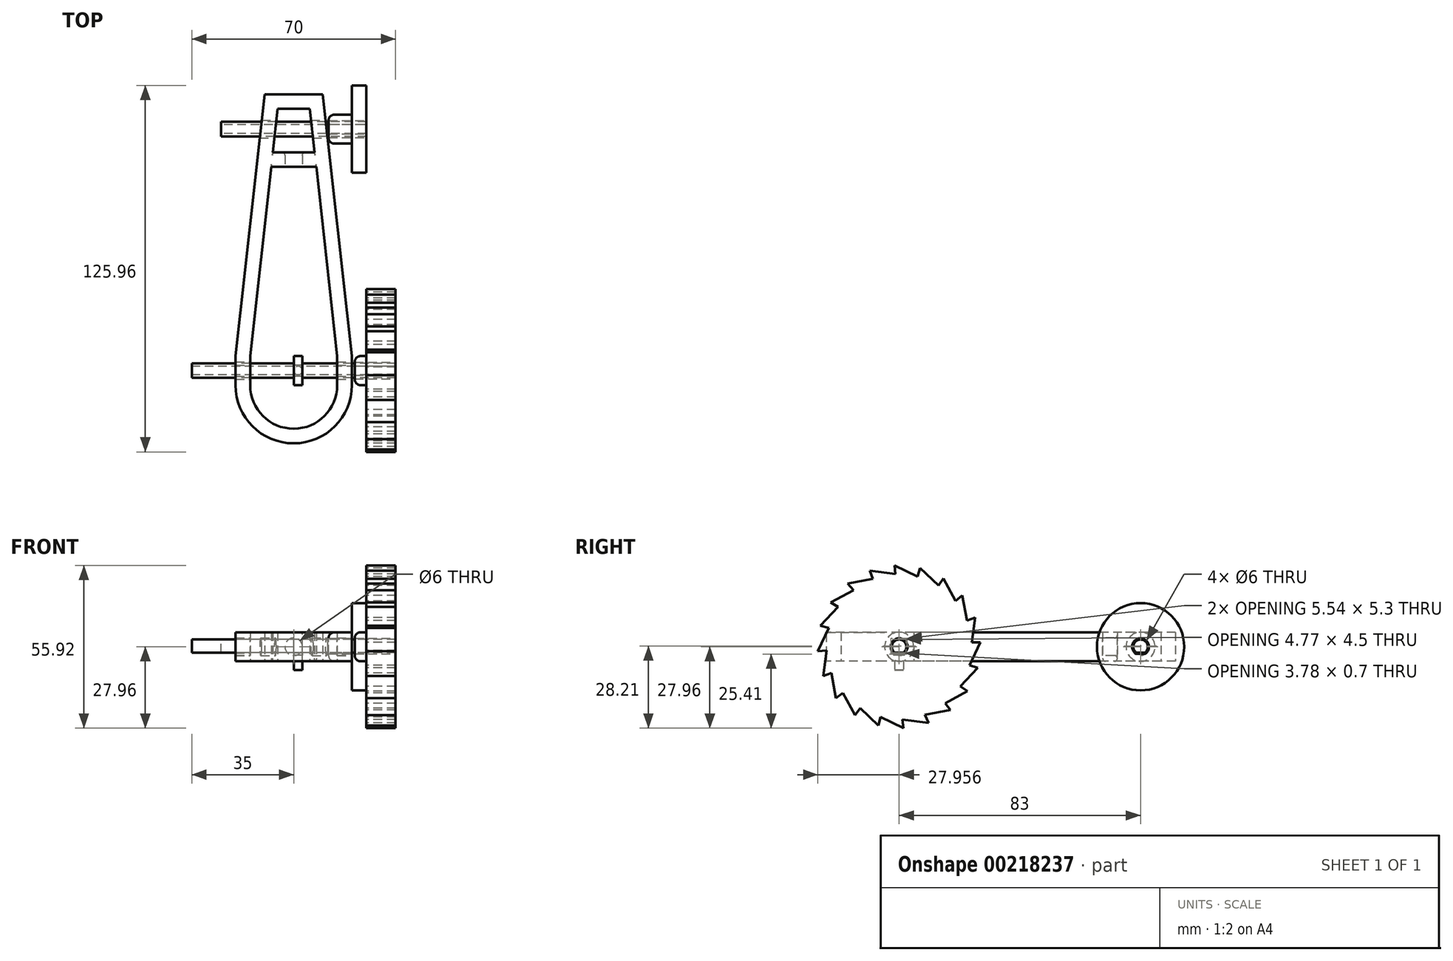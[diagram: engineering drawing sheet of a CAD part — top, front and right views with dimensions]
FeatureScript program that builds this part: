
annotation { "Feature Type Name" : "Feature", "Feature Type Description" : "" }
export const myFeature = defineFeature(function(context is Context, id is Id, definition is map)
    precondition{}
    {
        {
            var Q0;
            Q0=qCreatedBy(makeId("Top.planeOp"),FACE);
            var sketch = newSketch(context, id + "F0", { "sketchPlane" : qUnion([Q0])});
            skLineSegment(sketch, "E0.bottom", {"start": v(-20, -34.15) * mm, "end": v(20, -34.15) * mm});
            skLineSegment(sketch, "E0.top", {"start": v(-20, -44.15) * mm, "end": v(20, -44.15) * mm});
            skLineSegment(sketch, "E0.left", {"start": v(-20, -34.15) * mm, "end": v(-20, -44.15) * mm});
            skLineSegment(sketch, "E0.right", {"start": v(20, -34.15) * mm, "end": v(20, -44.15) * mm});
            skLineSegment(sketch, "E1.bottom", {"start": v(-10, 55.85) * mm, "end": v(10, 55.85) * mm});
            skLineSegment(sketch, "E1.top", {"start": v(-10, 50.85) * mm, "end": v(10, 50.85) * mm});
            skLineSegment(sketch, "E1.left", {"start": v(-10, 55.85) * mm, "end": v(-10, 50.85) * mm});
            skLineSegment(sketch, "E1.right", {"start": v(10, 55.85) * mm, "end": v(10, 50.85) * mm});
            skPoint(sketch, "E2", {"position": v(0, -34.15) * mm});
            skPoint(sketch, "E3", {"position": v(0, 50.85) * mm});
            skLineSegment(sketch, "E4", {"start": v(-10, 55.85) * mm, "end": v(-20, -34.15) * mm});
            skLineSegment(sketch, "E5", {"start": v(10, 55.85) * mm, "end": v(20, -34.15) * mm});
            skLineSegment(sketch, "E6", {"start": v(-5.52, 50.85) * mm, "end": v(-14.97, -34.15) * mm});
            skLineSegment(sketch, "E7", {"start": v(5.52, 50.85) * mm, "end": v(14.97, -34.15) * mm});
            skLineSegment(sketch, "E8.bottom", {"start": v(-7.75, 30.85) * mm, "end": v(7.75, 30.85) * mm});
            skLineSegment(sketch, "E8.top", {"start": v(-7.75, 35.85) * mm, "end": v(7.75, 35.85) * mm});
            skLineSegment(sketch, "E8.left", {"start": v(-7.75, 30.85) * mm, "end": v(-7.75, 35.85) * mm});
            skLineSegment(sketch, "E8.right", {"start": v(7.75, 30.85) * mm, "end": v(7.75, 35.85) * mm});
            skArc(sketch, "E9", {"start": v(-20, -44.15) * mm, "mid": v(0, -64.15) * mm, "end": v(20, -44.15) * mm});
            skLineSegment(sketch, "E10", {"start": v(-14.97, -34.15) * mm, "end": v(-14.97, -44.15) * mm});
            skLineSegment(sketch, "E11", {"start": v(14.97, -34.15) * mm, "end": v(14.97, -44.15) * mm});
            skArc(sketch, "E12", {"start": v(-14.97, -44.15) * mm, "mid": v(0, -59.12) * mm, "end": v(14.97, -44.15) * mm});
            skSolve(sketch);
        }
        {
            var Q0;
            {var subQ0=sQuery(id+"F0.wireOp",EDGE,"E0.left");Q0=makeQuery(id+"F0.imprint","IMPRINT",FACE,{"disambiguationData":[TD([[makeQuery(id+"F0.imprint","IMPRINT",EDGE,{"derivedFrom":subQ0}),1.0]])]});}
            var Q1;
            {var subQ0=sQuery(id+"F0.wireOp",EDGE,"E0.right");Q1=makeQuery(id+"F0.imprint","IMPRINT",FACE,{"disambiguationData":[TD([[makeQuery(id+"F0.imprint","IMPRINT",EDGE,{"derivedFrom":subQ0}),-1.0]])]});}
            var Q2;
            Q2=makeQuery(id+"F0.imprint","IMPRINT",FACE,{"disambiguationData":[TD([[makeQuery(id+"F0.imprint","IMPRINT",EDGE,{"derivedFrom":sQuery(id+"F0.wireOp",EDGE,"E1.bottom")}),-1.0]])]});
            var Q3;
            {var subQ1=sQuery(id+"F0.wireOp",EDGE,"E1.right");Q3=makeQuery(id+"F0.imprint","IMPRINT",FACE,{"disambiguationData":[TD([[makeQuery(id+"F0.imprint","IMPRINT",EDGE,{"derivedFrom":subQ1}),1.0]])]});}
            var Q4;
            {var subQ5=sQuery(id+"F0.wireOp",EDGE,"E1.left");Q4=makeQuery(id+"F0.imprint","IMPRINT",FACE,{"disambiguationData":[TD([[makeQuery(id+"F0.imprint","IMPRINT",EDGE,{"derivedFrom":subQ5}),-1.0]])]});}
            var Q5;
            {var subQ0=sQuery(id+"F0.wireOp",EDGE,"E8.bottom");Q5=makeQuery(id+"F0.imprint","IMPRINT",FACE,{"disambiguationData":[TD([[makeQuery(id+"F0.imprint","IMPRINT",EDGE,{"derivedFrom":subQ0}),1.0]])]});}
            var Q6;
            {var subQ0=sQuery(id+"F0.wireOp",EDGE,"E8.left");Q6=makeQuery(id+"F0.imprint","IMPRINT",FACE,{"disambiguationData":[TD([[makeQuery(id+"F0.imprint","IMPRINT",EDGE,{"derivedFrom":subQ0}),-1.0]])]});}
            var Q7;
            {var subQ0=sQuery(id+"F0.wireOp",EDGE,"E8.right");Q7=makeQuery(id+"F0.imprint","IMPRINT",FACE,{"disambiguationData":[TD([[makeQuery(id+"F0.imprint","IMPRINT",EDGE,{"derivedFrom":subQ0}),1.0]])]});}
            var Q8;
            {var subQ0=sQuery(id+"F0.wireOp",EDGE,"E9");Q8=makeQuery(id+"F0.imprint","IMPRINT",FACE,{"disambiguationData":[TD([[makeQuery(id+"F0.imprint","IMPRINT",EDGE,{"derivedFrom":subQ0}),1.0]])]});}
            extrude(context, id + "F1", {"entities" : qUnion([Q0, Q1, Q2, Q3, Q4, Q5, Q6, Q7, Q8]), "depth" : 10 * mm});
        }
        {
            var Q0;
            Q0=qCreatedBy(makeId("Right.planeOp"),FACE);
            var sketch = newSketch(context, id + "F2", { "sketchPlane" : qUnion([Q0])});
            skCircle(sketch, "E13", {"center": v(43.85, 5) * mm, "radius": 3 * mm});
            skCircle(sketch, "E14", {"center": v(-39.15, 5) * mm, "radius": 3 * mm});
            skCircle(sketch, "E15", {"center": v(-39.15, 5) * mm, "radius": 2.5 * mm});
            skLineSegment(sketch, "E16", {"start": v(-40.65, 3) * mm, "end": v(-37.65, 3) * mm});
            skCircle(sketch, "E17", {"center": v(43.85, 5) * mm, "radius": 2.5 * mm});
            skLineSegment(sketch, "E18", {"start": v(42.35, 3) * mm, "end": v(45.35, 3) * mm});
            skCircle(sketch, "E19", {"center": v(-39.15, 5) * mm, "radius": 5 * mm});
            skCircle(sketch, "E20", {"center": v(-39.15, 5) * mm, "radius": 2.9 * mm});
            skLineSegment(sketch, "E21", {"start": v(-37.26, 2.8) * mm, "end": v(-41.04, 2.8) * mm});
            skSolve(sketch);
        }
        {
            var Q0;
            Q0=makeQuery(id+"F2.imprint","IMPRINT",FACE,{"disambiguationData":[TD([[makeQuery(id+"F2.imprint","IMPRINT",EDGE,{"derivedFrom":sQuery(id+"F2.wireOp",EDGE,"E14")}),1.0]])]});
            var Q1;
            Q1=makeQuery(id+"F2.imprint","IMPRINT",FACE,{"disambiguationData":[TD([[makeQuery(id+"F2.imprint","IMPRINT",EDGE,{"derivedFrom":sQuery(id+"F2.wireOp",EDGE,"E13")}),1.0]])]});
            var Q2;
            {var subQ0=sQuery(id+"F2.wireOp",EDGE,"E16");Q2=makeQuery(id+"F2.imprint","IMPRINT",FACE,{"disambiguationData":[TD([[makeQuery(id+"F2.imprint","IMPRINT",EDGE,{"derivedFrom":subQ0}),1.0]])]});}
            var Q3;
            {var subQ0=sQuery(id+"F2.wireOp",EDGE,"E18");Q3=makeQuery(id+"F2.imprint","IMPRINT",FACE,{"disambiguationData":[TD([[makeQuery(id+"F2.imprint","IMPRINT",EDGE,{"derivedFrom":subQ0}),1.0]])]});}
            var Q4;
            {var subQ0=sQuery(id+"F2.wireOp",EDGE,"E18");Q4=makeQuery(id+"F2.imprint","IMPRINT",FACE,{"disambiguationData":[TD([[makeQuery(id+"F2.imprint","IMPRINT",EDGE,{"derivedFrom":subQ0}),-1.0]])]});}
            var Q5;
            {var subQ0=sQuery(id+"F2.wireOp",EDGE,"E16");var subQ1=sQuery(id+"F2.wireOp",EDGE,"E15");var subQ2=makeQuery(id+"F2.imprint","INTERSECT",VERTEX,{"disambiguationData":[OD(0.0)],"derivedFrom":[subQ1,subQ0]});Q5=makeQuery(id+"F2.imprint","IMPRINT",FACE,{"disambiguationData":[TD([[makeQuery(id+"F2.imprint","IMPRINT",EDGE,{"disambiguationData":[TD([[subQ2,-1.0]])],"derivedFrom":subQ1}),-1.0]])]});}
            var Q6;
            {var subQ0=sQuery(id+"F2.wireOp",EDGE,"E16");Q6=makeQuery(id+"F2.imprint","IMPRINT",FACE,{"disambiguationData":[TD([[makeQuery(id+"F2.imprint","IMPRINT",EDGE,{"derivedFrom":subQ0}),-1.0]])]});}
            var Q7;
            {var subQ0=sQuery(id+"F2.wireOp",EDGE,"E21");var subQ1=sQuery(id+"F2.wireOp",EDGE,"E15");var subQ2=makeQuery(id+"F2.imprint","INTERSECT",VERTEX,{"disambiguationData":[OD(0.0)],"derivedFrom":[subQ1,subQ0]});Q7=makeQuery(id+"F2.imprint","IMPRINT",FACE,{"disambiguationData":[TD([[makeQuery(id+"F2.imprint","IMPRINT",EDGE,{"disambiguationData":[TD([[subQ2,-1.0]])],"derivedFrom":subQ1}),-1.0]])]});}
            var Q8;
            {var subQ0=sQuery(id+"F2.wireOp",EDGE,"E21");var subQ1=sQuery(id+"F2.wireOp",EDGE,"E15");var subQ2=makeQuery(id+"F2.imprint","INTERSECT",VERTEX,{"disambiguationData":[OD(0.0)],"derivedFrom":[subQ1,subQ0]});Q8=makeQuery(id+"F2.imprint","IMPRINT",FACE,{"disambiguationData":[TD([[makeQuery(id+"F2.imprint","IMPRINT",EDGE,{"disambiguationData":[TD([[subQ2,-1.0]])],"derivedFrom":subQ1}),1.0]])]});}
            extrude(context, id + "F3", {"entities" : qUnion([Q0, Q1, Q2, Q3, Q4, Q5, Q6, Q7, Q8]), "operationType" : NewBodyOperationType.REMOVE, "oppositeDirection" : true, "depth" : 25 * mm, "hasSecondDirection" : true, "secondDirectionOppositeDirection" : false, "secondDirectionDepth" : 25 * mm});
        }
        {
            var Q0;
            Q0=makeQuery(id+"F1.opExtrude","SWEPT_FACE",FACE,{"disambiguationData":[OSD([sQuery(id+"F0.wireOp",EDGE,"E8.bottom")])]});
            var sketch = newSketch(context, id + "F4", { "sketchPlane" : qUnion([Q0])});
            skCircle(sketch, "E22", {"center": v(0, 5) * mm, "radius": 3 * mm});
            skPoint(sketch, "E22.centerSnap0", {"position": v(-7.75, 5) * mm});
            skSolve(sketch);
        }
        {
            var Q0;
            Q0=makeQuery(id+"F4.imprint","IMPRINT",FACE,{"disambiguationData":[TD([[makeQuery(id+"F4.imprint","IMPRINT",EDGE,{"derivedFrom":sQuery(id+"F4.wireOp",EDGE,"E22")}),1.0]])]});
            extrude(context, id + "F5", {"entities" : qUnion([Q0]), "operationType" : NewBodyOperationType.REMOVE, "oppositeDirection" : true, "depth" : 6 * mm});
        }
        {
            var Q0;
            Q0=makeQuery(id+"F5.boolean.opBoolean","COPY",EDGE,{"derivedFrom":makeQuery(id+"F5.opExtrude","CAP_EDGE",EDGE,{"disambiguationData":[OSD([sQuery(id+"F4.wireOp",EDGE,"E22")])],"isStart":true})});
            var Q1;
            Q1=makeQuery(id+"F5.boolean.opBoolean","INTERSECT",EDGE,{"derivedFrom":[makeQuery(id+"F1.opExtrude","SWEPT_FACE",FACE,{"disambiguationData":[OSD([sQuery(id+"F0.wireOp",EDGE,"E8.top")])]}),makeQuery(id+"F5.opExtrude","SWEPT_FACE",FACE,{"disambiguationData":[OSD([sQuery(id+"F4.wireOp",EDGE,"E22")])]})]});
            var Q2;
            Q2=makeQuery(id+"F1.opExtrude","CAP_EDGE",EDGE,{"disambiguationData":[OSD([sQuery(id+"F0.wireOp",EDGE,"E8.top")])],"isStart":true});
            var Q3;
            Q3=makeQuery(id+"F1.opExtrude","CAP_EDGE",EDGE,{"disambiguationData":[OSD([sQuery(id+"F0.wireOp",EDGE,"E8.bottom")])],"isStart":true});
            fillet(context, id + "F6", {"entities" : qUnion([Q0, Q1, Q2, Q3]), "radius" : 1 * mm, "tangentPropagation" : true, "allowEdgeOverflow" : false});
        }
        {
            var Q0;
            {var subQ0=sQuery(id+"F2.wireOp",EDGE,"E18");Q0=makeQuery(id+"F2.imprint","IMPRINT",FACE,{"disambiguationData":[TD([[makeQuery(id+"F2.imprint","IMPRINT",EDGE,{"derivedFrom":subQ0}),1.0]])]});}
            extrude(context, id + "F7", {"entities" : qUnion([Q0]), "depth" : 25 * mm, "hasSecondDirection" : true, "secondDirectionOppositeDirection" : true, "secondDirectionDepth" : 25 * mm});
        }
        {
            var Q0;
            {var subQ0=sQuery(id+"F2.wireOp",EDGE,"E16");Q0=makeQuery(id+"F2.imprint","IMPRINT",FACE,{"disambiguationData":[TD([[makeQuery(id+"F2.imprint","IMPRINT",EDGE,{"derivedFrom":subQ0}),1.0]])]});}
            extrude(context, id + "F8", {"entities" : qUnion([Q0]), "depth" : 35 * mm, "hasSecondDirection" : true, "secondDirectionOppositeDirection" : true, "secondDirectionDepth" : 35 * mm});
        }
        {
            var Q0;
            Q0=qCreatedBy(makeId("Right.planeOp"),FACE);
            cPlane(context, id + "F9", {"entities" : qUnion([Q0]), "cplaneType" : CPlaneType.OFFSET, "offset" : 25 * mm, "width" : 150 * mm, "height" : 150 * mm});
        }
        {
            var Q0;
            Q0=qCreatedBy(id+"F9.planeOp",FACE);
            var sketch = newSketch(context, id + "F10", { "sketchPlane" : qUnion([Q0])});
            skPoint(sketch, "E23.0", {"position": v(43.85, 5) * mm});
            skPoint(sketch, "E24.0", {"position": v(-39.15, 5) * mm});
            skCircle(sketch, "E25", {"center": v(-39.15, 5) * mm, "radius": 2.9 * mm});
            skLineSegment(sketch, "E26", {"start": v(-37.53, 2.6) * mm, "end": v(-40.78, 2.6) * mm});
            skCircle(sketch, "E27", {"center": v(-39.15, 5) * mm, "radius": 5 * mm});
            skCircle(sketch, "E28", {"center": v(-39.15, 5) * mm, "radius": 25 * mm});
            skCircle(sketch, "E29", {"center": v(43.85, 5) * mm, "radius": 2.9 * mm});
            skCircle(sketch, "E30", {"center": v(43.85, 5) * mm, "radius": 5 * mm});
            skCircle(sketch, "E31", {"center": v(43.85, 5) * mm, "radius": 15 * mm});
            skLineSegment(sketch, "E32", {"start": v(45.47, 2.6) * mm, "end": v(42.22, 2.6) * mm});
            skCircle(sketch, "E33.cCircle", {"center": v(-39.15, 5) * mm, "radius": 28 * mm, "construction": true});
            skLineSegment(sketch, "E33.0", {"start": v(-31.96, 32.06) * mm, "end": v(-23.95, 28.51) * mm});
            skLineSegment(sketch, "E33.1", {"start": v(-23.95, 28.51) * mm, "end": v(-17.43, 22.66) * mm});
            skLineSegment(sketch, "E33.2", {"start": v(-17.43, 22.66) * mm, "end": v(-13.03, 15.08) * mm});
            skLineSegment(sketch, "E33.3", {"start": v(-13.03, 15.08) * mm, "end": v(-11.2, 6.52) * mm});
            skLineSegment(sketch, "E33.4", {"start": v(-11.2, 6.52) * mm, "end": v(-12.1, -2.2) * mm});
            skLineSegment(sketch, "E33.5", {"start": v(-12.1, -2.2) * mm, "end": v(-15.64, -10.2) * mm});
            skLineSegment(sketch, "E33.6", {"start": v(-15.64, -10.2) * mm, "end": v(-21.5, -16.73) * mm});
            skLineSegment(sketch, "E33.7", {"start": v(-21.5, -16.73) * mm, "end": v(-29.07, -21.12) * mm});
            skLineSegment(sketch, "E33.8", {"start": v(-29.07, -21.12) * mm, "end": v(-37.64, -22.96) * mm});
            skLineSegment(sketch, "E33.9", {"start": v(-37.64, -22.96) * mm, "end": v(-46.35, -22.06) * mm});
            skLineSegment(sketch, "E33.10", {"start": v(-46.35, -22.06) * mm, "end": v(-54.36, -18.51) * mm});
            skLineSegment(sketch, "E33.11", {"start": v(-54.36, -18.51) * mm, "end": v(-60.88, -12.66) * mm});
            skLineSegment(sketch, "E33.12", {"start": v(-60.88, -12.66) * mm, "end": v(-65.28, -5.08) * mm});
            skLineSegment(sketch, "E33.13", {"start": v(-65.28, -5.08) * mm, "end": v(-67.11, 3.48) * mm});
            skLineSegment(sketch, "E33.14", {"start": v(-67.11, 3.48) * mm, "end": v(-66.21, 12.2) * mm});
            skLineSegment(sketch, "E33.15", {"start": v(-66.21, 12.2) * mm, "end": v(-62.66, 20.2) * mm});
            skLineSegment(sketch, "E33.16", {"start": v(-62.66, 20.2) * mm, "end": v(-56.82, 26.73) * mm});
            skLineSegment(sketch, "E33.17", {"start": v(-56.82, 26.73) * mm, "end": v(-49.24, 31.12) * mm});
            skLineSegment(sketch, "E33.18", {"start": v(-49.24, 31.12) * mm, "end": v(-40.67, 32.96) * mm});
            skLineSegment(sketch, "E33.19", {"start": v(-40.67, 32.96) * mm, "end": v(-31.96, 32.06) * mm});
            skLineSegment(sketch, "E34", {"start": v(-15.64, -10.2) * mm, "end": v(-18.16, -8.57) * mm});
            skLineSegment(sketch, "E35", {"start": v(-21.5, -16.73) * mm, "end": v(-23.36, -14.38) * mm});
            skLineSegment(sketch, "E36", {"start": v(-12.1, -2.2) * mm, "end": v(-14.98, -1.36) * mm});
            skLineSegment(sketch, "E37", {"start": v(-29.07, -21.12) * mm, "end": v(-30.24, -18.36) * mm});
            skLineSegment(sketch, "E38", {"start": v(-13.03, 15.08) * mm, "end": v(-15.85, 14.06) * mm});
            skLineSegment(sketch, "E39", {"start": v(-17.43, 22.66) * mm, "end": v(-19.76, 20.78) * mm});
            skLineSegment(sketch, "E40", {"start": v(-11.2, 6.52) * mm, "end": v(-14.2, 6.52) * mm});
            skLineSegment(sketch, "E41", {"start": v(-37.64, -22.96) * mm, "end": v(-37.99, -19.97) * mm});
            skLineSegment(sketch, "E42", {"start": v(-46.35, -22.06) * mm, "end": v(-45.52, -19.18) * mm});
            skLineSegment(sketch, "E43", {"start": v(-54.36, -18.51) * mm, "end": v(-52.53, -16.12) * mm});
            skLineSegment(sketch, "E44", {"start": v(-60.88, -12.66) * mm, "end": v(-58.48, -10.86) * mm});
            skLineSegment(sketch, "E45", {"start": v(-65.28, -5.08) * mm, "end": v(-62.48, -4) * mm});
            skLineSegment(sketch, "E46", {"start": v(-67.11, 3.48) * mm, "end": v(-64.12, 3.75) * mm});
            skLineSegment(sketch, "E47", {"start": v(-66.21, 12.2) * mm, "end": v(-63.32, 11.42) * mm});
            skLineSegment(sketch, "E48", {"start": v(-62.66, 20.2) * mm, "end": v(-60.09, 18.67) * mm});
            skLineSegment(sketch, "E49", {"start": v(-56.82, 26.73) * mm, "end": v(-54.84, 24.47) * mm});
            skLineSegment(sketch, "E50", {"start": v(-49.24, 31.12) * mm, "end": v(-48.17, 28.32) * mm});
            skLineSegment(sketch, "E51", {"start": v(-23.95, 28.51) * mm, "end": v(-25.63, 26.02) * mm});
            skLineSegment(sketch, "E52", {"start": v(-31.96, 32.06) * mm, "end": v(-32.81, 29.18) * mm});
            skLineSegment(sketch, "E53", {"start": v(-40.67, 32.96) * mm, "end": v(-40.5, 29.96) * mm});
            skLineSegment(sketch, "E54", {"start": v(-12.1, -2.2) * mm, "end": v(-18.16, -8.57) * mm});
            skLineSegment(sketch, "E55", {"start": v(-15.64, -10.2) * mm, "end": v(-23.36, -14.38) * mm});
            skLineSegment(sketch, "E56", {"start": v(-21.5, -16.73) * mm, "end": v(-30.24, -18.36) * mm});
            skLineSegment(sketch, "E57", {"start": v(-29.07, -21.12) * mm, "end": v(-37.99, -19.97) * mm});
            skLineSegment(sketch, "E58", {"start": v(-37.64, -22.96) * mm, "end": v(-45.52, -19.18) * mm});
            skLineSegment(sketch, "E59", {"start": v(-46.35, -22.06) * mm, "end": v(-52.53, -16.12) * mm});
            skLineSegment(sketch, "E60", {"start": v(-54.36, -18.51) * mm, "end": v(-58.48, -10.86) * mm});
            skLineSegment(sketch, "E61", {"start": v(-60.88, -12.66) * mm, "end": v(-62.48, -4) * mm});
            skLineSegment(sketch, "E62", {"start": v(-65.28, -5.08) * mm, "end": v(-64.12, 3.75) * mm});
            skLineSegment(sketch, "E63", {"start": v(-67.11, 3.48) * mm, "end": v(-63.32, 11.42) * mm});
            skLineSegment(sketch, "E64", {"start": v(-66.21, 12.2) * mm, "end": v(-60.09, 18.67) * mm});
            skLineSegment(sketch, "E65", {"start": v(-62.66, 20.2) * mm, "end": v(-54.84, 24.47) * mm});
            skLineSegment(sketch, "E66", {"start": v(-56.82, 26.73) * mm, "end": v(-48.17, 28.32) * mm});
            skLineSegment(sketch, "E67", {"start": v(-49.24, 31.12) * mm, "end": v(-40.5, 29.96) * mm});
            skLineSegment(sketch, "E68", {"start": v(-40.67, 32.96) * mm, "end": v(-32.81, 29.18) * mm});
            skLineSegment(sketch, "E69", {"start": v(-31.96, 32.06) * mm, "end": v(-25.63, 26.02) * mm});
            skLineSegment(sketch, "E70", {"start": v(-23.95, 28.51) * mm, "end": v(-19.76, 20.78) * mm});
            skLineSegment(sketch, "E71", {"start": v(-17.43, 22.66) * mm, "end": v(-15.85, 14.06) * mm});
            skLineSegment(sketch, "E72", {"start": v(-13.03, 15.08) * mm, "end": v(-14.2, 6.52) * mm});
            skLineSegment(sketch, "E73", {"start": v(-11.2, 6.52) * mm, "end": v(-14.98, -1.36) * mm});
            skSolve(sketch);
        }
        {
            var Q0;
            Q0=makeQuery(id+"F10.imprint","IMPRINT",FACE,{"disambiguationData":[TD([[makeQuery(id+"F10.imprint","IMPRINT",EDGE,{"derivedFrom":sQuery(id+"F10.wireOp",EDGE,"E30")}),1.0]])]});
            var Q1;
            {var subQ0=sQuery(id+"F10.wireOp",EDGE,"E32");Q1=makeQuery(id+"F10.imprint","IMPRINT",FACE,{"disambiguationData":[TD([[makeQuery(id+"F10.imprint","IMPRINT",EDGE,{"derivedFrom":subQ0}),1.0]])]});}
            extrude(context, id + "F11", {"entities" : qUnion([Q0, Q1]), "oppositeDirection" : true, "depth" : 13 * mm});
        }
        {
            var Q0;
            Q0=makeQuery(id+"F10.imprint","IMPRINT",FACE,{"disambiguationData":[TD([[makeQuery(id+"F10.imprint","IMPRINT",EDGE,{"derivedFrom":sQuery(id+"F10.wireOp",EDGE,"E30")}),-1.0]])]});
            extrude(context, id + "F12", {"entities" : qUnion([Q0]), "operationType" : NewBodyOperationType.ADD, "oppositeDirection" : true, "depth" : 5 * mm});
        }
        {
            var Q0;
            Q0=makeQuery(id+"F10.imprint","IMPRINT",FACE,{"disambiguationData":[TD([[makeQuery(id+"F10.imprint","IMPRINT",EDGE,{"derivedFrom":sQuery(id+"F10.wireOp",EDGE,"E27")}),1.0]])]});
            var Q1;
            {var subQ0=sQuery(id+"F10.wireOp",EDGE,"E26");Q1=makeQuery(id+"F10.imprint","IMPRINT",FACE,{"disambiguationData":[TD([[makeQuery(id+"F10.imprint","IMPRINT",EDGE,{"derivedFrom":subQ0}),1.0]])]});}
            extrude(context, id + "F13", {"entities" : qUnion([Q0, Q1]), "oppositeDirection" : true, "depth" : 4 * mm});
        }
        {
            var Q0;
            Q0=makeQuery(id+"F10.imprint","IMPRINT",FACE,{"disambiguationData":[TD([[makeQuery(id+"F10.imprint","IMPRINT",EDGE,{"derivedFrom":sQuery(id+"F10.wireOp",EDGE,"E27")}),-1.0]])]});
            var Q1;
            Q1=makeQuery(id+"F10.imprint","IMPRINT",FACE,{"disambiguationData":[TD([[makeQuery(id+"F10.imprint","IMPRINT",EDGE,{"derivedFrom":sQuery(id+"F10.wireOp",EDGE,"E27")}),1.0]])]});
            var Q2;
            {var subQ0=sQuery(id+"F10.wireOp",EDGE,"E26");Q2=makeQuery(id+"F10.imprint","IMPRINT",FACE,{"disambiguationData":[TD([[makeQuery(id+"F10.imprint","IMPRINT",EDGE,{"derivedFrom":subQ0}),1.0]])]});}
            var Q3;
            {var subQ0=sQuery(id+"F10.wireOp",EDGE,"E47");Q3=makeQuery(id+"F10.imprint","IMPRINT",FACE,{"disambiguationData":[TD([[makeQuery(id+"F10.imprint","IMPRINT",EDGE,{"derivedFrom":subQ0}),1.0]])]});}
            var Q4;
            {var subQ0=sQuery(id+"F10.wireOp",EDGE,"E48");Q4=makeQuery(id+"F10.imprint","IMPRINT",FACE,{"disambiguationData":[TD([[makeQuery(id+"F10.imprint","IMPRINT",EDGE,{"derivedFrom":subQ0}),1.0]])]});}
            var Q5;
            {var subQ0=sQuery(id+"F10.wireOp",EDGE,"E49");Q5=makeQuery(id+"F10.imprint","IMPRINT",FACE,{"disambiguationData":[TD([[makeQuery(id+"F10.imprint","IMPRINT",EDGE,{"derivedFrom":subQ0}),1.0]])]});}
            var Q6;
            {var subQ0=sQuery(id+"F10.wireOp",EDGE,"E50");Q6=makeQuery(id+"F10.imprint","IMPRINT",FACE,{"disambiguationData":[TD([[makeQuery(id+"F10.imprint","IMPRINT",EDGE,{"derivedFrom":subQ0}),1.0]])]});}
            var Q7;
            {var subQ0=sQuery(id+"F10.wireOp",EDGE,"E46");Q7=makeQuery(id+"F10.imprint","IMPRINT",FACE,{"disambiguationData":[TD([[makeQuery(id+"F10.imprint","IMPRINT",EDGE,{"derivedFrom":subQ0}),1.0]])]});}
            var Q8;
            {var subQ0=sQuery(id+"F10.wireOp",EDGE,"E45");Q8=makeQuery(id+"F10.imprint","IMPRINT",FACE,{"disambiguationData":[TD([[makeQuery(id+"F10.imprint","IMPRINT",EDGE,{"derivedFrom":subQ0}),1.0]])]});}
            var Q9;
            {var subQ0=sQuery(id+"F10.wireOp",EDGE,"E44");Q9=makeQuery(id+"F10.imprint","IMPRINT",FACE,{"disambiguationData":[TD([[makeQuery(id+"F10.imprint","IMPRINT",EDGE,{"derivedFrom":subQ0}),1.0]])]});}
            var Q10;
            {var subQ0=sQuery(id+"F10.wireOp",EDGE,"E43");Q10=makeQuery(id+"F10.imprint","IMPRINT",FACE,{"disambiguationData":[TD([[makeQuery(id+"F10.imprint","IMPRINT",EDGE,{"derivedFrom":subQ0}),1.0]])]});}
            var Q11;
            {var subQ0=sQuery(id+"F10.wireOp",EDGE,"E42");Q11=makeQuery(id+"F10.imprint","IMPRINT",FACE,{"disambiguationData":[TD([[makeQuery(id+"F10.imprint","IMPRINT",EDGE,{"derivedFrom":subQ0}),1.0]])]});}
            var Q12;
            {var subQ0=sQuery(id+"F10.wireOp",EDGE,"E41");Q12=makeQuery(id+"F10.imprint","IMPRINT",FACE,{"disambiguationData":[TD([[makeQuery(id+"F10.imprint","IMPRINT",EDGE,{"derivedFrom":subQ0}),1.0]])]});}
            var Q13;
            {var subQ0=sQuery(id+"F10.wireOp",EDGE,"E37");Q13=makeQuery(id+"F10.imprint","IMPRINT",FACE,{"disambiguationData":[TD([[makeQuery(id+"F10.imprint","IMPRINT",EDGE,{"derivedFrom":subQ0}),1.0]])]});}
            var Q14;
            {var subQ0=sQuery(id+"F10.wireOp",EDGE,"E35");Q14=makeQuery(id+"F10.imprint","IMPRINT",FACE,{"disambiguationData":[TD([[makeQuery(id+"F10.imprint","IMPRINT",EDGE,{"derivedFrom":subQ0}),1.0]])]});}
            var Q15;
            {var subQ0=sQuery(id+"F10.wireOp",EDGE,"E34");Q15=makeQuery(id+"F10.imprint","IMPRINT",FACE,{"disambiguationData":[TD([[makeQuery(id+"F10.imprint","IMPRINT",EDGE,{"derivedFrom":subQ0}),1.0]])]});}
            var Q16;
            {var subQ2=sQuery(id+"F10.wireOp",EDGE,"E36");Q16=makeQuery(id+"F10.imprint","IMPRINT",FACE,{"disambiguationData":[TD([[makeQuery(id+"F10.imprint","IMPRINT",EDGE,{"derivedFrom":subQ2}),1.0]])]});}
            var Q17;
            {var subQ2=sQuery(id+"F10.wireOp",EDGE,"E40");Q17=makeQuery(id+"F10.imprint","IMPRINT",FACE,{"disambiguationData":[TD([[makeQuery(id+"F10.imprint","IMPRINT",EDGE,{"derivedFrom":subQ2}),1.0]])]});}
            var Q18;
            {var subQ0=sQuery(id+"F10.wireOp",EDGE,"E38");Q18=makeQuery(id+"F10.imprint","IMPRINT",FACE,{"disambiguationData":[TD([[makeQuery(id+"F10.imprint","IMPRINT",EDGE,{"derivedFrom":subQ0}),1.0]])]});}
            var Q19;
            {var subQ2=sQuery(id+"F10.wireOp",EDGE,"E39");Q19=makeQuery(id+"F10.imprint","IMPRINT",FACE,{"disambiguationData":[TD([[makeQuery(id+"F10.imprint","IMPRINT",EDGE,{"derivedFrom":subQ2}),1.0]])]});}
            var Q20;
            {var subQ2=sQuery(id+"F10.wireOp",EDGE,"E51");Q20=makeQuery(id+"F10.imprint","IMPRINT",FACE,{"disambiguationData":[TD([[makeQuery(id+"F10.imprint","IMPRINT",EDGE,{"derivedFrom":subQ2}),1.0]])]});}
            var Q21;
            {var subQ2=sQuery(id+"F10.wireOp",EDGE,"E52");Q21=makeQuery(id+"F10.imprint","IMPRINT",FACE,{"disambiguationData":[TD([[makeQuery(id+"F10.imprint","IMPRINT",EDGE,{"derivedFrom":subQ2}),1.0]])]});}
            var Q22;
            {var subQ2=sQuery(id+"F10.wireOp",EDGE,"E53");Q22=makeQuery(id+"F10.imprint","IMPRINT",FACE,{"disambiguationData":[TD([[makeQuery(id+"F10.imprint","IMPRINT",EDGE,{"derivedFrom":subQ2}),1.0]])]});}
            extrude(context, id + "F14", {"entities" : qUnion([Q0, Q1, Q2, Q3, Q4, Q5, Q6, Q7, Q8, Q9, Q10, Q11, Q12, Q13, Q14, Q15, Q16, Q17, Q18, Q19, Q20, Q21, Q22]), "operationType" : NewBodyOperationType.ADD, "depth" : 10 * mm});
        }
        {
            var Q0;
            Q0=makeQuery(id+"F11.opExtrude","CAP_EDGE",EDGE,{"disambiguationData":[OSD([sQuery(id+"F10.wireOp",EDGE,"E30")])],"isStart":false});
            var Q1;
            Q1=makeQuery(id+"F13.opExtrude","CAP_EDGE",EDGE,{"disambiguationData":[OSD([sQuery(id+"F10.wireOp",EDGE,"E27")])],"isStart":false});
            fillet(context, id + "F15", {"entities" : qUnion([Q0, Q1]), "radius" : 2 * mm, "tangentPropagation" : true, "allowEdgeOverflow" : false});
        }
        {
            var Q0;
            Q0=makeQuery(id+"F2.imprint","IMPRINT",FACE,{"disambiguationData":[TD([[makeQuery(id+"F2.imprint","IMPRINT",EDGE,{"derivedFrom":sQuery(id+"F2.wireOp",EDGE,"E14")}),-1.0]])]});
            var Q1;
            {var subQ0=sQuery(id+"F2.wireOp",EDGE,"E21");var subQ1=sQuery(id+"F2.wireOp",EDGE,"E15");var subQ2=makeQuery(id+"F2.imprint","INTERSECT",VERTEX,{"disambiguationData":[OD(0.0)],"derivedFrom":[subQ1,subQ0]});Q1=makeQuery(id+"F2.imprint","IMPRINT",FACE,{"disambiguationData":[TD([[makeQuery(id+"F2.imprint","IMPRINT",EDGE,{"disambiguationData":[TD([[subQ2,-1.0]])],"derivedFrom":subQ1}),-1.0]])]});}
            var Q2;
            {var subQ0=sQuery(id+"F2.wireOp",EDGE,"E21");var subQ1=sQuery(id+"F2.wireOp",EDGE,"E15");var subQ2=makeQuery(id+"F2.imprint","INTERSECT",VERTEX,{"disambiguationData":[OD(0.0)],"derivedFrom":[subQ1,subQ0]});Q2=makeQuery(id+"F2.imprint","IMPRINT",FACE,{"disambiguationData":[TD([[makeQuery(id+"F2.imprint","IMPRINT",EDGE,{"disambiguationData":[TD([[subQ2,-1.0]])],"derivedFrom":subQ1}),1.0]])]});}
            var Q3;
            Q3=makeQuery(id+"F2.imprint","IMPRINT",FACE,{"disambiguationData":[TD([[makeQuery(id+"F2.imprint","IMPRINT",EDGE,{"derivedFrom":sQuery(id+"F2.wireOp",EDGE,"E14")}),1.0]])]});
            extrude(context, id + "F16", {"entities" : qUnion([Q0, Q1, Q2, Q3]), "operationType" : NewBodyOperationType.ADD, "depth" : 3 * mm});
        }
        {
            var Q0;
            Q0=qCreatedBy(makeId("Top.planeOp"),FACE);
            var sketch = newSketch(context, id + "F17", { "sketchPlane" : qUnion([Q0])});
            skPoint(sketch, "E74.0", {"position": v(0, -39.15) * mm});
            skCircle(sketch, "E75", {"center": v(1.5, -39.15) * mm, "radius": 1.5 * mm});
            skSolve(sketch);
        }
        {
            var Q0;
            Q0=makeQuery(id+"F17.imprint","IMPRINT",FACE,{"disambiguationData":[TD([[makeQuery(id+"F17.imprint","IMPRINT",EDGE,{"derivedFrom":sQuery(id+"F17.wireOp",EDGE,"E75")}),1.0]])]});
            extrude(context, id + "F18", {"entities" : qUnion([Q0]), "operationType" : NewBodyOperationType.ADD, "depth" : 1 * mm, "hasSecondDirection" : true, "secondDirectionOppositeDirection" : true, "secondDirectionDepth" : 3 * mm});
        }
    });
